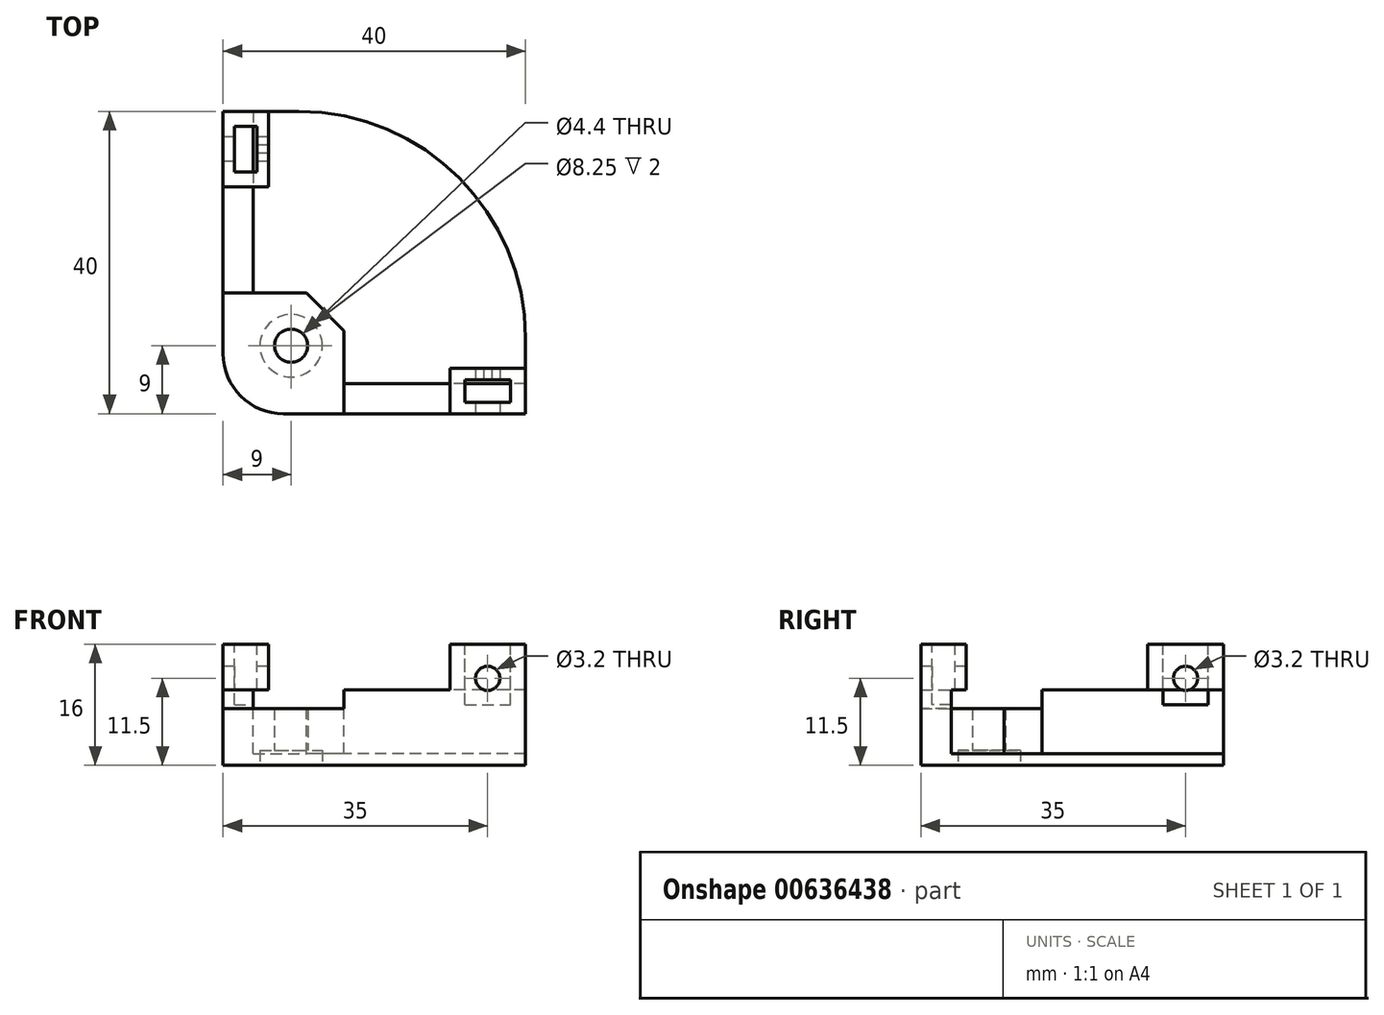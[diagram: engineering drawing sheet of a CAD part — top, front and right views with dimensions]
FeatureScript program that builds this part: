
annotation { "Feature Type Name" : "Feature", "Feature Type Description" : "" }
export const myFeature = defineFeature(function(context is Context, id is Id, definition is map)
    precondition{}
    {
        {
            var Q0;
            Q0=qCreatedBy(makeId("Top.planeOp"),FACE);
            var sketch = newSketch(context, id + "F0", { "sketchPlane" : qUnion([Q0])});
            skLineSegment(sketch, "E0.bottom", {"start": v(0, 0) * mm, "end": v(40, 0) * mm});
            skLineSegment(sketch, "E0.top", {"start": v(0, 40) * mm, "end": v(40, 40) * mm});
            skLineSegment(sketch, "E0.left", {"start": v(0, 0) * mm, "end": v(0, 40) * mm});
            skLineSegment(sketch, "E0.right", {"start": v(40, 0) * mm, "end": v(40, 40) * mm});
            skSolve(sketch);
        }
        {
            var Q0;
            Q0 = qSketchRegion(id + "F0", true);
            extrude(context, id + "F1", {"entities" : qUnion([Q0]), "depth" : 10 * mm, "offsetDistance" : 25 * mm});
        }
        {
            var Q0;
            Q0=makeQuery(id+"F1.opExtrude","CAP_FACE",FACE,{"disambiguationData":[OSD([sQuery(id+"F0.wireOp",EDGE,"E0.bottom"),sQuery(id+"F0.wireOp",EDGE,"E0.top"),sQuery(id+"F0.wireOp",EDGE,"E0.left"),sQuery(id+"F0.wireOp",EDGE,"E0.right")])],"isStart":false});
            var sketch = newSketch(context, id + "F2", { "sketchPlane" : qUnion([Q0])});
            skLineSegment(sketch, "E1.bottom", {"start": v(40, 40) * mm, "end": v(4, 40) * mm});
            skLineSegment(sketch, "E1.top", {"start": v(40, 4) * mm, "end": v(16, 4) * mm});
            skLineSegment(sketch, "E1.left", {"start": v(40, 40) * mm, "end": v(40, 4) * mm});
            skLineSegment(sketch, "E1.right", {"start": v(4, 40) * mm, "end": v(4, 16) * mm});
            skLineSegment(sketch, "E2", {"start": v(4, 16) * mm, "end": v(11, 16) * mm});
            skLineSegment(sketch, "E3", {"start": v(16, 11) * mm, "end": v(16, 4) * mm});
            skLineSegment(sketch, "E4", {"start": v(16, 11) * mm, "end": v(11, 16) * mm});
            skPoint(sketch, "E5.orphan", {"position": v(16, 16) * mm});
            skSolve(sketch);
        }
        {
            var Q0;
            Q0 = qSketchRegion(id + "F2", true);
            extrude(context, id + "F3", {"entities" : qUnion([Q0]), "operationType" : NewBodyOperationType.REMOVE, "oppositeDirection" : true, "depth" : 8.5 * mm, "offsetDistance" : 25 * mm});
        }
        {
            var Q0;
            Q0=makeQuery(id+"F1.opExtrude","CAP_FACE",FACE,{"disambiguationData":[OSD([sQuery(id+"F0.wireOp",EDGE,"E0.bottom"),sQuery(id+"F0.wireOp",EDGE,"E0.top"),sQuery(id+"F0.wireOp",EDGE,"E0.left"),sQuery(id+"F0.wireOp",EDGE,"E0.right")])],"isStart":false});
            var sketch = newSketch(context, id + "F4", { "sketchPlane" : qUnion([Q0])});
            skLineSegment(sketch, "E6.bottom", {"start": v(0, 0) * mm, "end": v(16, 0) * mm});
            skLineSegment(sketch, "E6.top", {"start": v(0, 16) * mm, "end": v(16, 16) * mm});
            skLineSegment(sketch, "E6.left", {"start": v(0, 0) * mm, "end": v(0, 16) * mm});
            skLineSegment(sketch, "E6.right", {"start": v(16, 0) * mm, "end": v(16, 16) * mm});
            skSolve(sketch);
        }
        {
            var Q0;
            Q0 = qSketchRegion(id + "F4", true);
            extrude(context, id + "F5", {"entities" : qUnion([Q0]), "operationType" : NewBodyOperationType.REMOVE, "oppositeDirection" : true, "depth" : 2.5 * mm, "offsetDistance" : 25 * mm});
        }
        {
            var Q0;
            Q0=makeQuery(id+"F1.opExtrude","CAP_FACE",FACE,{"disambiguationData":[OSD([sQuery(id+"F0.wireOp",EDGE,"E0.bottom"),sQuery(id+"F0.wireOp",EDGE,"E0.top"),sQuery(id+"F0.wireOp",EDGE,"E0.left"),sQuery(id+"F0.wireOp",EDGE,"E0.right")])],"isStart":true});
            var sketch = newSketch(context, id + "F6", { "sketchPlane" : qUnion([Q0])});
            skPoint(sketch, "E7", {"position": v(9, -9) * mm});
            skSolve(sketch);
        }
        {
            var Q0;
            Q0=sQuery(id+"F6.wireOp",VERTEX,"E7");
            var Q1;
            Q1=makeQuery(id+"F1.opExtrude","SWEPT_BODY",BODY,{"disambiguationData":[OSD([sQuery(id+"F0.wireOp",EDGE,"E0.bottom"),sQuery(id+"F0.wireOp",EDGE,"E0.top"),sQuery(id+"F0.wireOp",EDGE,"E0.left"),sQuery(id+"F0.wireOp",EDGE,"E0.right")])]});
            hole(context, id + "F7", {"style" : HoleStyle.C_BORE, "endStyle" : HoleEndStyle.THROUGH, "holeDiameter" : 4.4 * mm, "cBoreDiameter" : 8.25 * mm, "cBoreDepth" : 2 * mm, "majorDiameter" : 5 * mm, "isTappedThrough" : true, "tappedDepth" : 12 * mm, "tapClearance" : 3, "locations" : qUnion([Q0]), "scope" : qUnion([Q1])});
        }
        {
            var Q0;
            {var subQ0=sQuery(id+"F0.wireOp",EDGE,"E0.top");var subQ1=sQuery(id+"F0.wireOp",EDGE,"E0.left");Q0=makeQuery(id+"F5.boolean.opBoolean","SPLIT",FACE,{"disambiguationData":[TD([makeQuery(id+"F1.opExtrude","SWEPT_FACE",FACE,{"disambiguationData":[OSD([subQ0])]})])],"derivedFrom":makeQuery(id+"F1.opExtrude","CAP_FACE",FACE,{"disambiguationData":[OSD([sQuery(id+"F0.wireOp",EDGE,"E0.bottom"),subQ0,subQ1,sQuery(id+"F0.wireOp",EDGE,"E0.right")])],"isStart":false})});}
            var sketch = newSketch(context, id + "F8", { "sketchPlane" : qUnion([Q0])});
            skLineSegment(sketch, "E8.bottom", {"start": v(0, 40) * mm, "end": v(6, 40) * mm});
            skLineSegment(sketch, "E8.top", {"start": v(0, 30) * mm, "end": v(6, 30) * mm});
            skLineSegment(sketch, "E8.left", {"start": v(0, 40) * mm, "end": v(0, 30) * mm});
            skLineSegment(sketch, "E8.right", {"start": v(6, 40) * mm, "end": v(6, 30) * mm});
            skLineSegment(sketch, "E9.bottom", {"start": v(40, 0) * mm, "end": v(30, 0) * mm});
            skLineSegment(sketch, "E9.top", {"start": v(40, 6) * mm, "end": v(30, 6) * mm});
            skLineSegment(sketch, "E9.left", {"start": v(40, 0) * mm, "end": v(40, 6) * mm});
            skLineSegment(sketch, "E9.right", {"start": v(30, 0) * mm, "end": v(30, 6) * mm});
            skSolve(sketch);
        }
        {
            var Q0;
            Q0 = qSketchRegion(id + "F8", true);
            extrude(context, id + "F9", {"entities" : qUnion([Q0]), "operationType" : NewBodyOperationType.ADD, "depth" : 6 * mm, "offsetDistance" : 25 * mm});
        }
        {
            var Q0;
            Q0=makeQuery(id+"F1.opExtrude","SWEPT_FACE",FACE,{"disambiguationData":[OSD([sQuery(id+"F0.wireOp",EDGE,"E0.left")])]});
            var sketch = newSketch(context, id + "F10", { "sketchPlane" : qUnion([Q0])});
            skPoint(sketch, "E10", {"position": v(-35, 11.5) * mm});
            skSolve(sketch);
        }
        {
            var Q0;
            Q0=sQuery(id+"F10.wireOp",VERTEX,"E10");
            var Q1;
            Q1=makeQuery(id+"F1.opExtrude","SWEPT_BODY",BODY,{"disambiguationData":[OSD([sQuery(id+"F0.wireOp",EDGE,"E0.bottom"),sQuery(id+"F0.wireOp",EDGE,"E0.top"),sQuery(id+"F0.wireOp",EDGE,"E0.left"),sQuery(id+"F0.wireOp",EDGE,"E0.right")])]});
            hole(context, id + "F11", {"style" : HoleStyle.SIMPLE, "endStyle" : HoleEndStyle.THROUGH, "holeDiameter" : 3.2 * mm, "majorDiameter" : 5 * mm, "isTappedThrough" : true, "tappedDepth" : 12 * mm, "tapClearance" : 3, "locations" : qUnion([Q0]), "scope" : qUnion([Q1])});
        }
        {
            var Q0;
            Q0=makeQuery(id+"F9.opExtrude","CAP_FACE",FACE,{"disambiguationData":[OSD([sQuery(id+"F8.wireOp",EDGE,"E8.bottom"),sQuery(id+"F8.wireOp",EDGE,"E8.top"),sQuery(id+"F8.wireOp",EDGE,"E8.left"),sQuery(id+"F8.wireOp",EDGE,"E8.right")])],"isStart":false});
            var sketch = newSketch(context, id + "F12", { "sketchPlane" : qUnion([Q0])});
            skLineSegment(sketch, "E11.bottom", {"start": v(1.5, 38) * mm, "end": v(4.5, 38) * mm});
            skLineSegment(sketch, "E11.top", {"start": v(1.5, 32) * mm, "end": v(4.5, 32) * mm});
            skLineSegment(sketch, "E11.left", {"start": v(1.5, 38) * mm, "end": v(1.5, 32) * mm});
            skLineSegment(sketch, "E11.right", {"start": v(4.5, 38) * mm, "end": v(4.5, 32) * mm});
            skLineSegment(sketch, "E12.bottom", {"start": v(38, 4.5) * mm, "end": v(32, 4.5) * mm});
            skLineSegment(sketch, "E12.top", {"start": v(38, 1.5) * mm, "end": v(32, 1.5) * mm});
            skLineSegment(sketch, "E12.left", {"start": v(38, 4.5) * mm, "end": v(38, 1.5) * mm});
            skLineSegment(sketch, "E12.right", {"start": v(32, 4.5) * mm, "end": v(32, 1.5) * mm});
            skSolve(sketch);
        }
        {
            var Q0;
            Q0 = qSketchRegion(id + "F12", true);
            extrude(context, id + "F13", {"entities" : qUnion([Q0]), "operationType" : NewBodyOperationType.REMOVE, "oppositeDirection" : true, "depth" : 8 * mm, "offsetDistance" : 25 * mm});
        }
        {
            var Q0;
            Q0=makeQuery(id+"F9.boolean.opBoolean","MERGE",FACE,{"derivedFrom":[makeQuery(id+"F1.opExtrude","SWEPT_FACE",FACE,{"disambiguationData":[OSD([sQuery(id+"F0.wireOp",EDGE,"E0.bottom")])]}),makeQuery(id+"F9.opExtrude","SWEPT_FACE",FACE,{"disambiguationData":[OSD([sQuery(id+"F8.wireOp",EDGE,"E9.bottom")])]})]});
            var sketch = newSketch(context, id + "F14", { "sketchPlane" : qUnion([Q0])});
            skPoint(sketch, "E13", {"position": v(35, 11.5) * mm});
            skSolve(sketch);
        }
        {
            var Q0;
            Q0=sQuery(id+"F14.wireOp",VERTEX,"E13");
            var Q1;
            Q1=makeQuery(id+"F1.opExtrude","SWEPT_BODY",BODY,{"disambiguationData":[OSD([sQuery(id+"F0.wireOp",EDGE,"E0.bottom"),sQuery(id+"F0.wireOp",EDGE,"E0.top"),sQuery(id+"F0.wireOp",EDGE,"E0.left"),sQuery(id+"F0.wireOp",EDGE,"E0.right")])]});
            hole(context, id + "F15", {"style" : HoleStyle.SIMPLE, "endStyle" : HoleEndStyle.THROUGH, "holeDiameter" : 3.2 * mm, "majorDiameter" : 5 * mm, "isTappedThrough" : true, "tappedDepth" : 12 * mm, "tapClearance" : 3, "locations" : qUnion([Q0]), "scope" : qUnion([Q1])});
        }
        {
            var Q0;
            Q0=makeQuery(id+"F1.opExtrude","SWEPT_EDGE",EDGE,{"disambiguationData":[OSD([sQuery(id+"F0.wireOp",EDGE,"E0.top"),sQuery(id+"F0.wireOp",EDGE,"E0.right")])]});
            fillet(context, id + "F16", {"entities" : qUnion([Q0]), "radius" : 30 * mm, "tangentPropagation" : true, "allowEdgeOverflow" : false});
        }
        {
            var Q0;
            Q0=makeQuery(id+"F1.opExtrude","SWEPT_EDGE",EDGE,{"disambiguationData":[OSD([sQuery(id+"F0.wireOp",EDGE,"E0.bottom"),sQuery(id+"F0.wireOp",EDGE,"E0.left")])]});
            fillet(context, id + "F17", {"entities" : qUnion([Q0]), "radius" : 8 * mm, "tangentPropagation" : true, "allowEdgeOverflow" : false});
        }
    });
